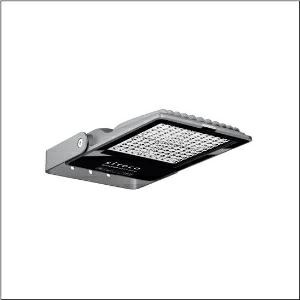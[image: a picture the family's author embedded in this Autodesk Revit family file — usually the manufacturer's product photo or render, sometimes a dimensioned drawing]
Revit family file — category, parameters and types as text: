
# Revit family: sicompact_r__31_mini___pl32_5xa7571b2k23_8fae
name_source: partatom
category: Lighting Fixtures
units: mm (PartAtom-declared; Revit-internal decimal feet)

## family parameters
Cut with Voids When Loaded = No
Host = Face
Light Source = No
Part Type = Normal
Room Calculation Point = No
Round Connector Dimension = Use Diameter
Shared = No

## types (1)
- SiCompact® 31 mini  PL32 (1 x LED, 8000 lm, 47 W, 4000K)
    Apparent Load = 47 VA
    CIE Flux Codes = 32 69 98 100 100
    Color Rendering = 70
    Color Temperature = 4000K
    Default Elevation = 1800 mm
    Description = SiCompact® 31 mini, floodlight, primary light control with lens, of plastic, of toughened safety glass, transparent, light distribution: PL32, light emission: direct distribution, primary light characteristic: asymmetric, installation type: surface-mounted, LED, High Power LED, rated luminous flux: 8.000lm, luminous efficacy: 170lm/W, light colour: 740, colour temperature: 4000K, control gear: ECG, with cable, 3x 1.5mm², mains connection: 220..240V, AC, 50/60Hz, connection cable pre-assembled, cable length: 2m, rated input power: 47W, of diecast aluminium, specular, metallic grey (RAL 9006), length: 461mm, width: 261mm, height: 62mm, bracket, of sheet steel, coated, metallic grey (RAL 9006), ON/OFF, protection rating (complete): IP66, insulation class (complete): insulation class I (protective earthing), certification: CE, ENEC, impact resistance: IK08, permissible operating ambient temperature: -40..+45°C, packaging unit: 1 piece

Light Distribution: PL32
    Height = 62 mm  [stored 0.203412 ft]
    Lamp = 1 x LED
    Lamp Light Flux = 8000 lm
    Lamp Power = 47 W
    Lamp count = 1
    Length = 460 mm
    Luminous efficacy = 170 lm/W
    Manufacturer = Siteco
    ModVariant = No
    Model = 5XA7571B2K23
    Mounting Place = Wall
    Mounting Type = Surface mounted
    Number of Poles = 1
    OnlyDefault = Yes
    Power Factor = 1
    Product Name = SiCompact® 31 mini | PL32
    Product group = floodlight | wall mounted
    ProductGroupID = 2001
    Protection Class = Protection class I
    Protection Degree = IP 66
    RLX_Detail_Level = 1
    RLX_Emergency_Light_Flux = 0 lm
    RLX_Emergency_Type = 0
    RLX_Emergency_Type_DB = No
    RlxData = <blob elided: 126177 chars, md5=c7f55b28>
    Socket = socket
    Standby Power = 0 W
    System Light Flux = 8000 lm
    System Power = 47 W
    Type Comments = Product without accessories
    Type Image = l_1006951.jpg
    URL = http://relux.com
    VarID = ---
    Voltage = 0 V
    Weight = 0.00 kg
    Width = 260 mm

note: [stored X ft] marks values corroborated as IEEE doubles in the binary element streams (Revit-internal decimal feet)

## geometry (parser evidence)
native form markers: Blend x4, Sweep x14
no freeform markers — native parametric forms only
